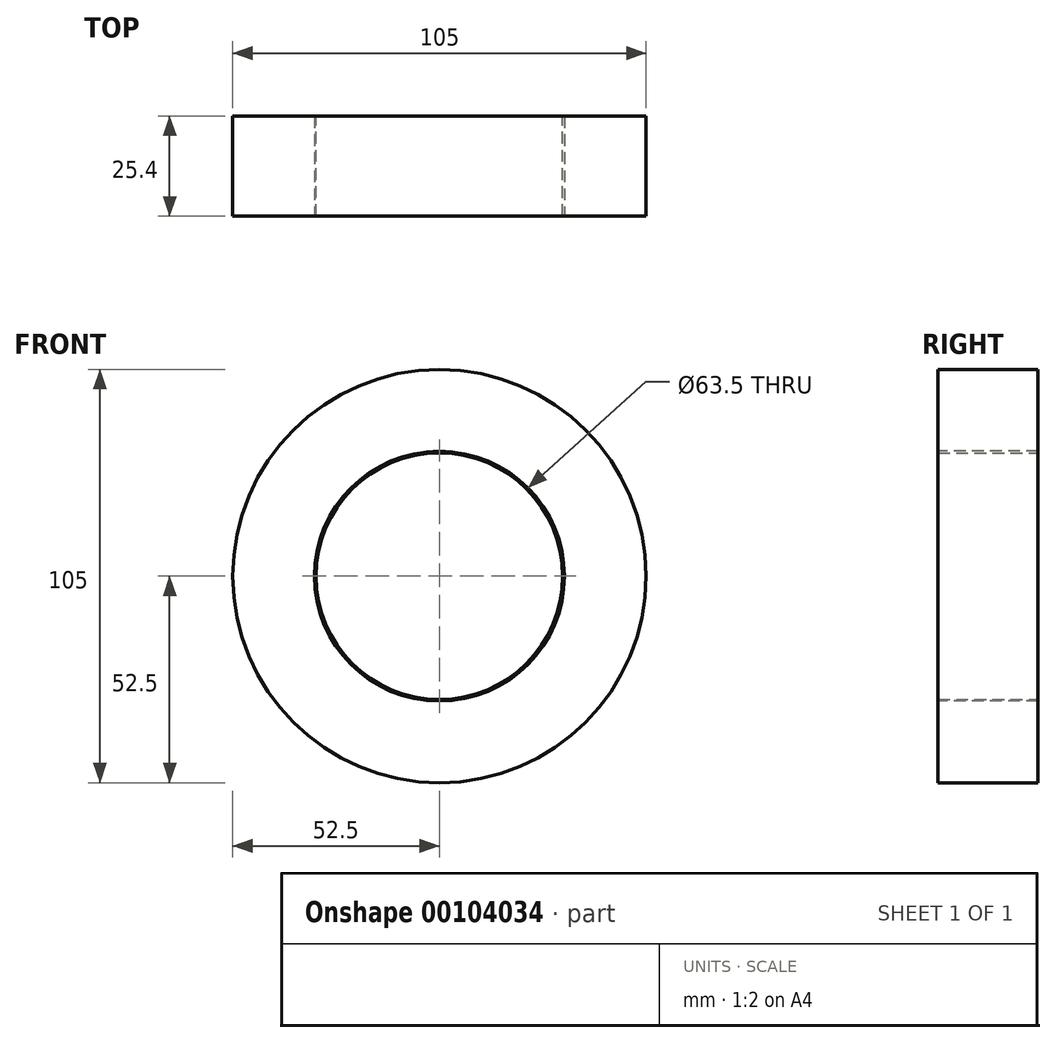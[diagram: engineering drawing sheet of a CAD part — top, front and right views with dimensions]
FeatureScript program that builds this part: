
annotation { "Feature Type Name" : "Feature", "Feature Type Description" : "" }
export const myFeature = defineFeature(function(context is Context, id is Id, definition is map)
    precondition{}
    {
        {
            var Q0;
            Q0=qCreatedBy(makeId("Front.planeOp"),FACE);
            var sketch = newSketch(context, id + "F0", { "sketchPlane" : qUnion([Q0])});
            skCircle(sketch, "E0", {"center": v(0, 0) * mm, "radius": 52.5 * mm});
            skSolve(sketch);
        }
        {
            var Q0;
            Q0=makeQuery(id+"F0.imprint","IMPRINT",FACE,{"disambiguationData":[TD([[makeQuery(id+"F0.imprint","IMPRINT",EDGE,{"derivedFrom":sQuery(id+"F0.wireOp",EDGE,"E0")}),1.0]])]});
            extrude(context, id + "F1", {"entities" : qUnion([Q0]), "depth" : 25.4 * mm});
        }
        {
            var Q0;
            Q0=makeQuery(id+"F1.opExtrude","CAP_FACE",FACE,{"disambiguationData":[OSD([sQuery(id+"F0.wireOp",EDGE,"E0")])],"isStart":false});
            var sketch = newSketch(context, id + "F2", { "sketchPlane" : qUnion([Q0])});
            skCircle(sketch, "E1", {"center": v(0, 0) * mm, "radius": 25.98 * mm});
            skSolve(sketch);
        }
        {
            var Q0;
            Q0=sQuery(id+"F2.wireOp",VERTEX,"E1.center");
            var Q1;
            Q1=makeQuery(id+"F1.opExtrude","SWEPT_BODY",BODY,{"disambiguationData":[OSD([sQuery(id+"F0.wireOp",EDGE,"E0")])]});
            hole(context, id + "F3", {"style" : HoleStyle.SIMPLE, "endStyle" : HoleEndStyle.THROUGH, "holeDiameter" : 63.5 * mm, "locations" : qUnion([Q0]), "scope" : qUnion([Q1]), "isTappedThrough" : true});
        }
        {
            var Q0;
            Q0=qCreatedBy(makeId("Front.planeOp"),FACE);
            var sketch = newSketch(context, id + "F4", { "sketchPlane" : qUnion([Q0])});
            skCircle(sketch, "E2", {"center": v(0, 0) * mm, "radius": 31.33 * mm});
            skSolve(sketch);
        }
        {
            var Q0;
            Q0=makeQuery(id+"F4.imprint","IMPRINT",FACE,{"disambiguationData":[TD([[makeQuery(id+"F4.imprint","IMPRINT",EDGE,{"derivedFrom":sQuery(id+"F4.wireOp",EDGE,"E2")}),1.0]])]});
            extrude(context, id + "F5", {"entities" : qUnion([Q0]), "depth" : 25.4 * mm});
        }
        {
            var Q0;
            Q0=qCreatedBy(makeId("Front.planeOp"),FACE);
            var sketch = newSketch(context, id + "F6", { "sketchPlane" : qUnion([Q0])});
            skCircle(sketch, "E3", {"center": v(0, 0) * mm, "radius": 20 * mm});
            skSolve(sketch);
        }
        {
            var Q0;
            Q0=makeQuery(id+"F6.imprint","IMPRINT",FACE,{"disambiguationData":[TD([[makeQuery(id+"F6.imprint","IMPRINT",EDGE,{"derivedFrom":sQuery(id+"F6.wireOp",EDGE,"E3")}),1.0]])]});
            extrude(context, id + "F7", {"entities" : qUnion([Q0]), "operationType" : NewBodyOperationType.REMOVE, "oppositeDirection" : true, "depth" : 25.4 * mm});
        }
    });
